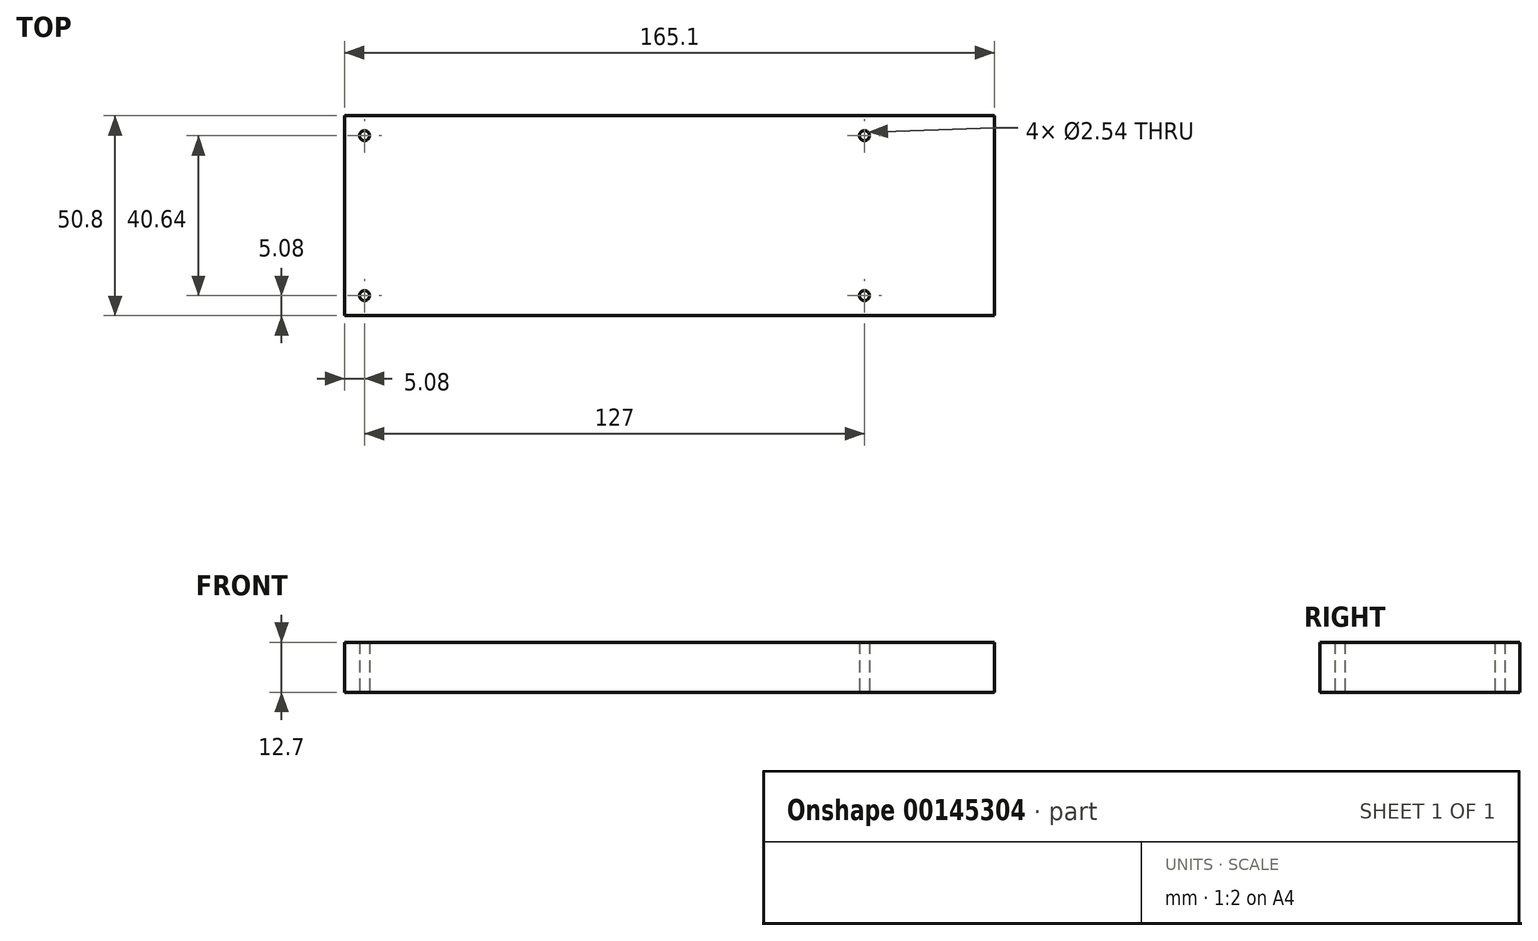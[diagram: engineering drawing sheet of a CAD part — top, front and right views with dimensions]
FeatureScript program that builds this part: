
annotation { "Feature Type Name" : "Feature", "Feature Type Description" : "" }
export const myFeature = defineFeature(function(context is Context, id is Id, definition is map)
    precondition{}
    {
        {
            var Q0;
            Q0=qCreatedBy(makeId("Top.planeOp"),FACE);
            var sketch = newSketch(context, id + "F0", { "sketchPlane" : qUnion([Q0])});
            skLineSegment(sketch, "E0.bottom", {"start": v(-82.55, 25.4) * mm, "end": v(82.55, 25.4) * mm});
            skLineSegment(sketch, "E0.top", {"start": v(-82.55, -25.4) * mm, "end": v(82.55, -25.4) * mm});
            skLineSegment(sketch, "E0.left", {"start": v(-82.55, 25.4) * mm, "end": v(-82.55, -25.4) * mm});
            skLineSegment(sketch, "E0.right", {"start": v(82.55, 25.4) * mm, "end": v(82.55, -25.4) * mm});
            skPoint(sketch, "E0.middle", {"position": v(0, 0) * mm});
            skCircle(sketch, "E1", {"center": v(-77.47, 20.32) * mm, "radius": 1.27 * mm});
            skCircle(sketch, "E2", {"center": v(-77.47, -20.32) * mm, "radius": 1.27 * mm});
            skCircle(sketch, "E3.1.0.0", {"center": v(49.53, 20.32) * mm, "radius": 1.27 * mm});
            skCircle(sketch, "E3.1.0.1", {"center": v(49.53, -20.32) * mm, "radius": 1.27 * mm});
            skLineSegment(sketch, "E3.direction1", {"start": v(-77.47, 20.32) * mm, "end": v(49.53, 20.32) * mm, "construction": true});
            skSolve(sketch);
        }
        {
            var Q0;
            Q0 = qSketchRegion(id + "F0", true);
            extrude(context, id + "F1", {"entities" : qUnion([Q0]), "depth" : 12.7 * mm});
        }
    });
